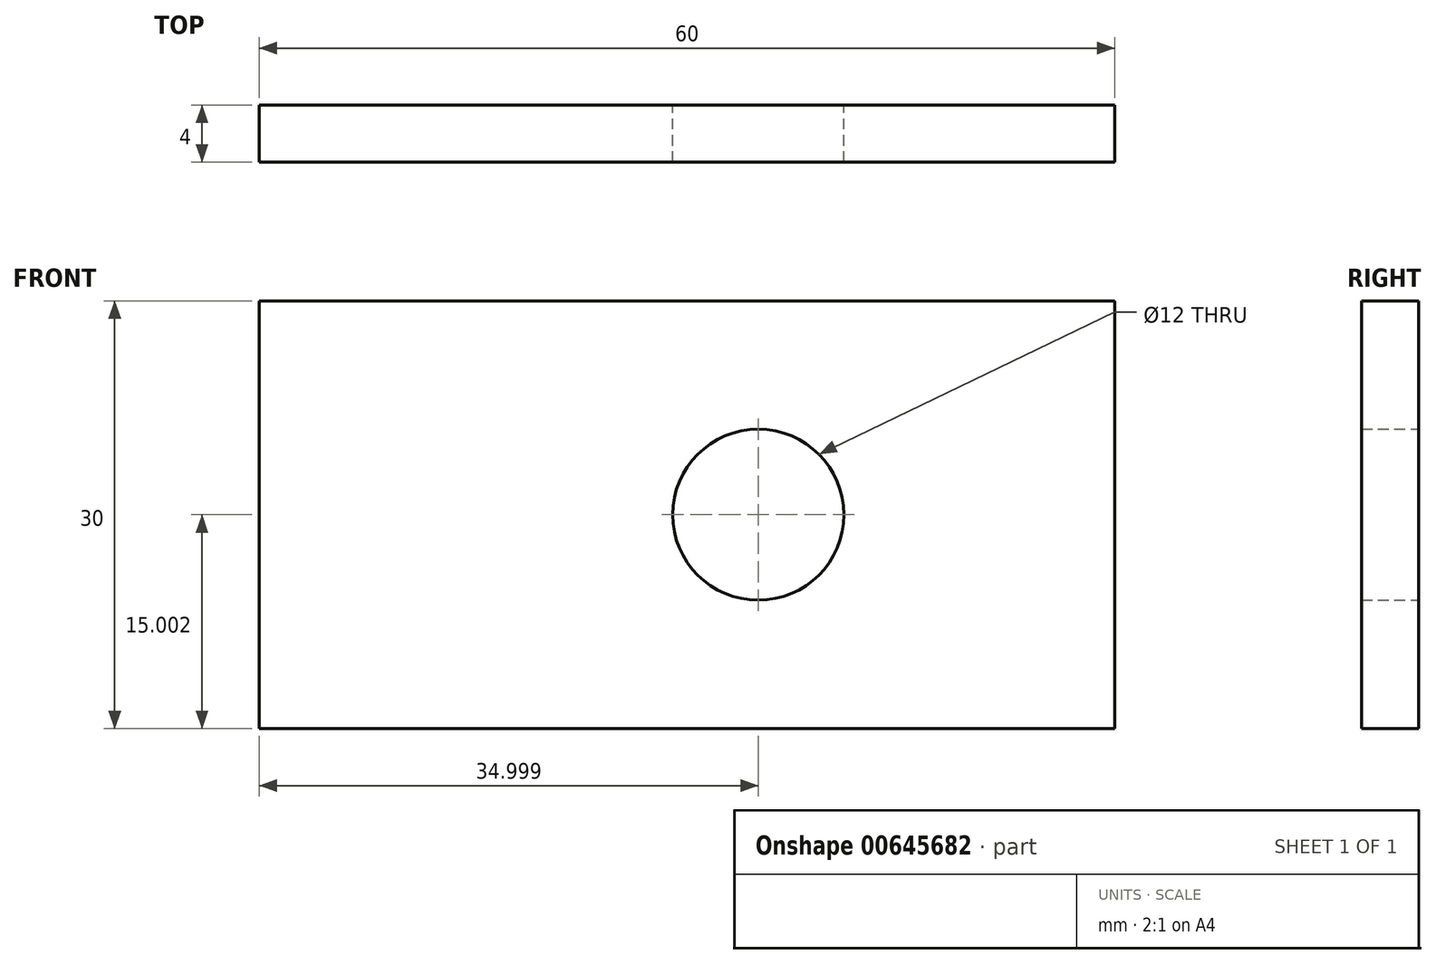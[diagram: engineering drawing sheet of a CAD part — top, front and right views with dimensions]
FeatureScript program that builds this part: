
annotation { "Feature Type Name" : "Feature", "Feature Type Description" : "" }
export const myFeature = defineFeature(function(context is Context, id is Id, definition is map)
    precondition{}
    {
        {
            var Q0;
            Q0=qCreatedBy(makeId("Front.planeOp"),FACE);
            var sketch = newSketch(context, id + "F0", { "sketchPlane" : qUnion([Q0])});
            skLineSegment(sketch, "E0.bottom", {"start": v(-29.74, 8.36) * mm, "end": v(30.26, 8.36) * mm});
            skLineSegment(sketch, "E0.top", {"start": v(-29.74, -21.64) * mm, "end": v(30.26, -21.64) * mm});
            skLineSegment(sketch, "E0.left", {"start": v(-29.74, 8.36) * mm, "end": v(-29.74, -21.64) * mm});
            skLineSegment(sketch, "E0.right", {"start": v(30.26, 8.36) * mm, "end": v(30.26, -21.64) * mm});
            skLineSegment(sketch, "E1", {"start": v(30.26, -6.64) * mm, "end": v(-29.74, -6.64) * mm, "construction": true});
            skCircle(sketch, "E2", {"center": v(5.26, -6.64) * mm, "radius": 6 * mm});
            skSolve(sketch);
        }
        {
            var Q0;
            Q0 = qSketchRegion(id + "F0", true);
            extrude(context, id + "F1", {"entities" : qUnion([Q0]), "depth" : 4 * mm, "offsetDistance" : 25 * mm});
        }
    });
